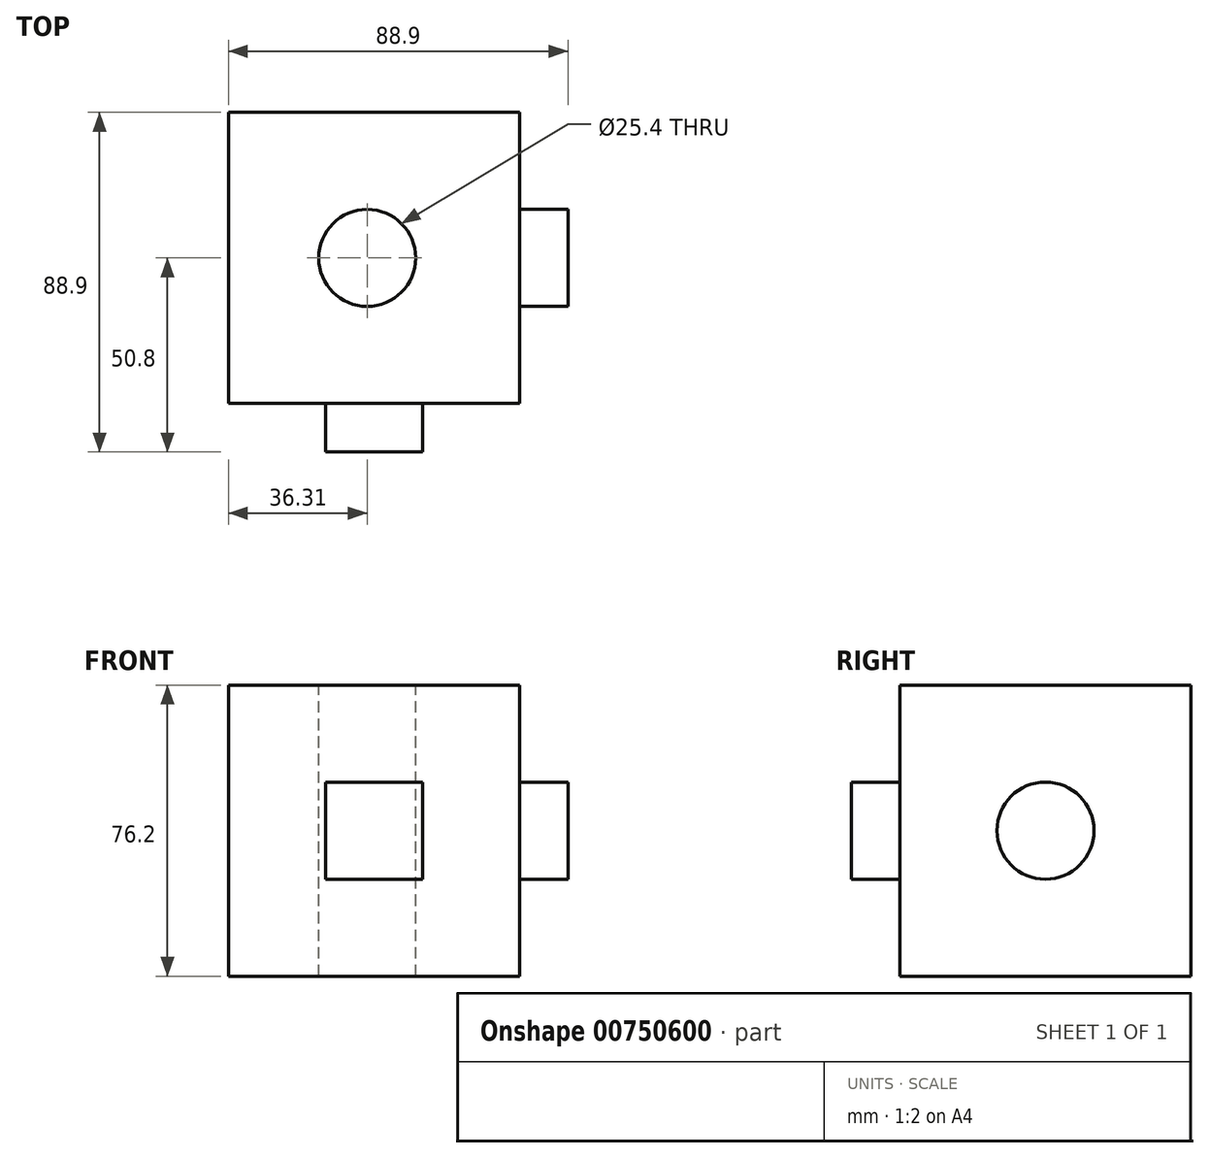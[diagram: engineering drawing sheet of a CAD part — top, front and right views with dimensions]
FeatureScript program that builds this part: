
annotation { "Feature Type Name" : "Feature", "Feature Type Description" : "" }
export const myFeature = defineFeature(function(context is Context, id is Id, definition is map)
    precondition{}
    {
        {
            var Q0;
            Q0=qCreatedBy(makeId("Front.planeOp"),FACE);
            var sketch = newSketch(context, id + "F0", { "sketchPlane" : qUnion([Q0])});
            skLineSegment(sketch, "E0.bottom", {"start": v(-36.3, -34.22) * mm, "end": v(39.9, -34.22) * mm});
            skLineSegment(sketch, "E0.top", {"start": v(-36.3, 41.98) * mm, "end": v(39.9, 41.98) * mm});
            skLineSegment(sketch, "E0.left", {"start": v(-36.3, -34.22) * mm, "end": v(-36.3, 41.98) * mm});
            skLineSegment(sketch, "E0.right", {"start": v(39.9, -34.22) * mm, "end": v(39.9, 41.98) * mm});
            skSolve(sketch);
        }
        {
            var Q0;
            Q0=makeQuery(id+"F0.imprint","IMPRINT",FACE,{"disambiguationData":[TD([[makeQuery(id+"F0.imprint","IMPRINT",EDGE,{"derivedFrom":sQuery(id+"F0.wireOp",EDGE,"E0.bottom")}),1.0]])]});
            extrude(context, id + "F1", {"entities" : qUnion([Q0]), "depth" : 76.2 * mm, "offsetDistance" : 25.4 * mm});
        }
        {
            var Q0;
            Q0=makeQuery(id+"F1.opExtrude","CAP_FACE",FACE,{"disambiguationData":[OSD([sQuery(id+"F0.wireOp",EDGE,"E0.bottom"),sQuery(id+"F0.wireOp",EDGE,"E0.top"),sQuery(id+"F0.wireOp",EDGE,"E0.left"),sQuery(id+"F0.wireOp",EDGE,"E0.right")])],"isStart":false});
            var sketch = newSketch(context, id + "F2", { "sketchPlane" : qUnion([Q0])});
            skLineSegment(sketch, "E1.bottom", {"start": v(-10.9, -8.82) * mm, "end": v(14.5, -8.82) * mm});
            skLineSegment(sketch, "E1.top", {"start": v(-10.9, 16.58) * mm, "end": v(14.5, 16.58) * mm});
            skLineSegment(sketch, "E1.left", {"start": v(-10.9, -8.82) * mm, "end": v(-10.9, 16.58) * mm});
            skLineSegment(sketch, "E1.right", {"start": v(14.5, -8.82) * mm, "end": v(14.5, 16.58) * mm});
            skSolve(sketch);
        }
        {
            var Q0;
            Q0=makeQuery(id+"F2.imprint","IMPRINT",FACE,{"disambiguationData":[TD([[makeQuery(id+"F2.imprint","IMPRINT",EDGE,{"derivedFrom":sQuery(id+"F2.wireOp",EDGE,"E1.bottom")}),1.0]])]});
            extrude(context, id + "F3", {"entities" : qUnion([Q0]), "operationType" : NewBodyOperationType.ADD, "depth" : 12.7 * mm, "offsetDistance" : 25.4 * mm});
        }
        {
            var Q0;
            Q0=makeQuery(id+"F1.opExtrude","SWEPT_FACE",FACE,{"disambiguationData":[OSD([sQuery(id+"F0.wireOp",EDGE,"E0.right")])]});
            var sketch = newSketch(context, id + "F4", { "sketchPlane" : qUnion([Q0])});
            skCircle(sketch, "E2", {"center": v(-38.1, 3.88) * mm, "radius": 12.7 * mm});
            skSolve(sketch);
        }
        {
            var Q0;
            Q0=makeQuery(id+"F4.imprint","IMPRINT",FACE,{"disambiguationData":[TD([[makeQuery(id+"F4.imprint","IMPRINT",EDGE,{"derivedFrom":sQuery(id+"F4.wireOp",EDGE,"E2")}),1.0]])]});
            extrude(context, id + "F5", {"entities" : qUnion([Q0]), "operationType" : NewBodyOperationType.ADD, "depth" : 12.7 * mm, "offsetDistance" : 25.4 * mm});
        }
        {
            var Q0;
            Q0=makeQuery(id+"F1.opExtrude","SWEPT_FACE",FACE,{"disambiguationData":[OSD([sQuery(id+"F0.wireOp",EDGE,"E0.top")])]});
            var sketch = newSketch(context, id + "F6", { "sketchPlane" : qUnion([Q0])});
            skPoint(sketch, "E3", {"position": v(0, -38.1) * mm});
            skSolve(sketch);
        }
        {
            var Q0;
            Q0=sQuery(id+"F6.wireOp",VERTEX,"E3");
            var Q1;
            Q1=makeQuery(id+"F1.opExtrude","SWEPT_BODY",BODY,{"disambiguationData":[OSD([sQuery(id+"F0.wireOp",EDGE,"E0.bottom"),sQuery(id+"F0.wireOp",EDGE,"E0.top"),sQuery(id+"F0.wireOp",EDGE,"E0.left"),sQuery(id+"F0.wireOp",EDGE,"E0.right")])]});
            hole(context, id + "F7", {"style" : HoleStyle.SIMPLE, "endStyle" : HoleEndStyle.THROUGH, "holeDiameter" : 25.4 * mm, "majorDiameter" : 6.35 * mm, "isTappedThrough" : true, "tappedDepth" : 12.7 * mm, "tapClearance" : 3, "locations" : qUnion([Q0]), "scope" : qUnion([Q1])});
        }
    });
